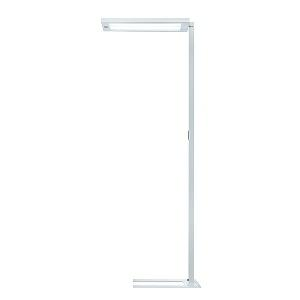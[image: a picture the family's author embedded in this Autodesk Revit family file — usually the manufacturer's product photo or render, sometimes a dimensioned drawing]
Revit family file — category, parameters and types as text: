
# Revit family: lavigo_-_dps_14000_840_d_g2_00803269_564a
name_source: partatom
category: Lighting Fixtures
units: mm (PartAtom-declared; Revit-internal decimal feet)

## family parameters
Cut with Voids When Loaded = No
Host = Face
Light Source = No
Part Type = Normal
Room Calculation Point = No
Round Connector Dimension = Use Diameter
Shared = No

## types (1)
- LAVIGO - DPS 14000/840/D/G2 (1 x LED, 14050 lm, 4000K)
    Apparent Load = 93 VA
    Approval mark = CE
    CIE Flux Codes = 60 87 97 12 100
    Color Rendering = 80-89
    Color Temperature = 4000K
    Control Gear = Electronic ballast
    Default Elevation = 1800 mm
    Description = DPS 14000/840/D/G2|Free-standing luminaire|light source: LED|work equipment: Electronic ballast|connected load: 220-240 V, 50/60 Hz|Power consumption: approx. 93 W|standby: approx. 0,50|power factor: approx. 0,943|luminous flux: 14050 lm|luminous efficacy: 151 lm/W|light distribution: Direct/indirect|direct ratio: approx. 13 %|colour temperature: Cold white, ca. 4000 K|color rendering index (CRI): >= 80|chromaticity tolerance:  3 SDCM|technology: Continuously dimmable|operation: Multi-function switch|luminaire body|material: Steel/plastic|surface: Painted|colour: White|lamp cover: Acrylic (PMMA), Satine|tubular section|material: Steel tube|surface: Painted|Form: Tubular section upright|colour of tubular section: White|luminaire base|Form: C-form flat|weight (net): approx. 19.7 kg|mains lead: 3.00 m Mains plug CEE 7/VII|Fastening: Floor standing base|decorative contrast side parts: Flint grey|glare control: Prism aperture|luminance(L65): <= 3000 cd/m|unified glare rating(4H 8H): <=  16|special features: Luminaire head detachable, Cradle to Cradle Certified TM, Direct light component with edge light and light-guide technology for homogenous light exit, Flicker-free, Separated, direct and indirect light individually adjustable|Approval mark: VDE - ENEC|
    Frequency = 50 Hz
    Height = 36 mm
    Lamp = 1 x LED
    Lamp Light Flux = 14050 lm
    Lamp count = 1
    Length = 675 mm
    Luminous efficacy = 151 lm/W
    Manufacturer = Waldmann
    ModVariant = No
    Model = 00803269
    Mounting Place = Floor
    Mounting Type = Freestanding
    Number of Poles = 1
    OnlyDefault = Yes
    Power Factor = 1
    Product Name = LAVIGO - DPS 14000/840/D/G2
    Product group = Free standing luminaire
    ProductGroupID = 13
    Protection Class = Protection class I
    Protection Degree = IP 20
    RLX_Detail_Level = 1
    RLX_Emergency_Light_Flux = 0 lm
    RLX_Emergency_Type = 0
    RLX_Emergency_Type_DB = No
    RlxData = <blob elided: 36677 chars, md5=ace2ab4e>
    Socket = socket
    Standby Power = 0 W
    System Light Flux = 14050 lm
    System Power = 93 W
    Type Comments = Product without accessories
    Type Image = 121695000-00610208.jpg
    URL = http://relux.com
    VarID = ---
    Voltage = 230 V
    Voltage Range = 220-240 V
    Weight = 0.00 kg
    Width = 320 mm

## geometry (parser evidence)
native form markers: Blend x4, Sweep x15
no freeform markers — native parametric forms only
